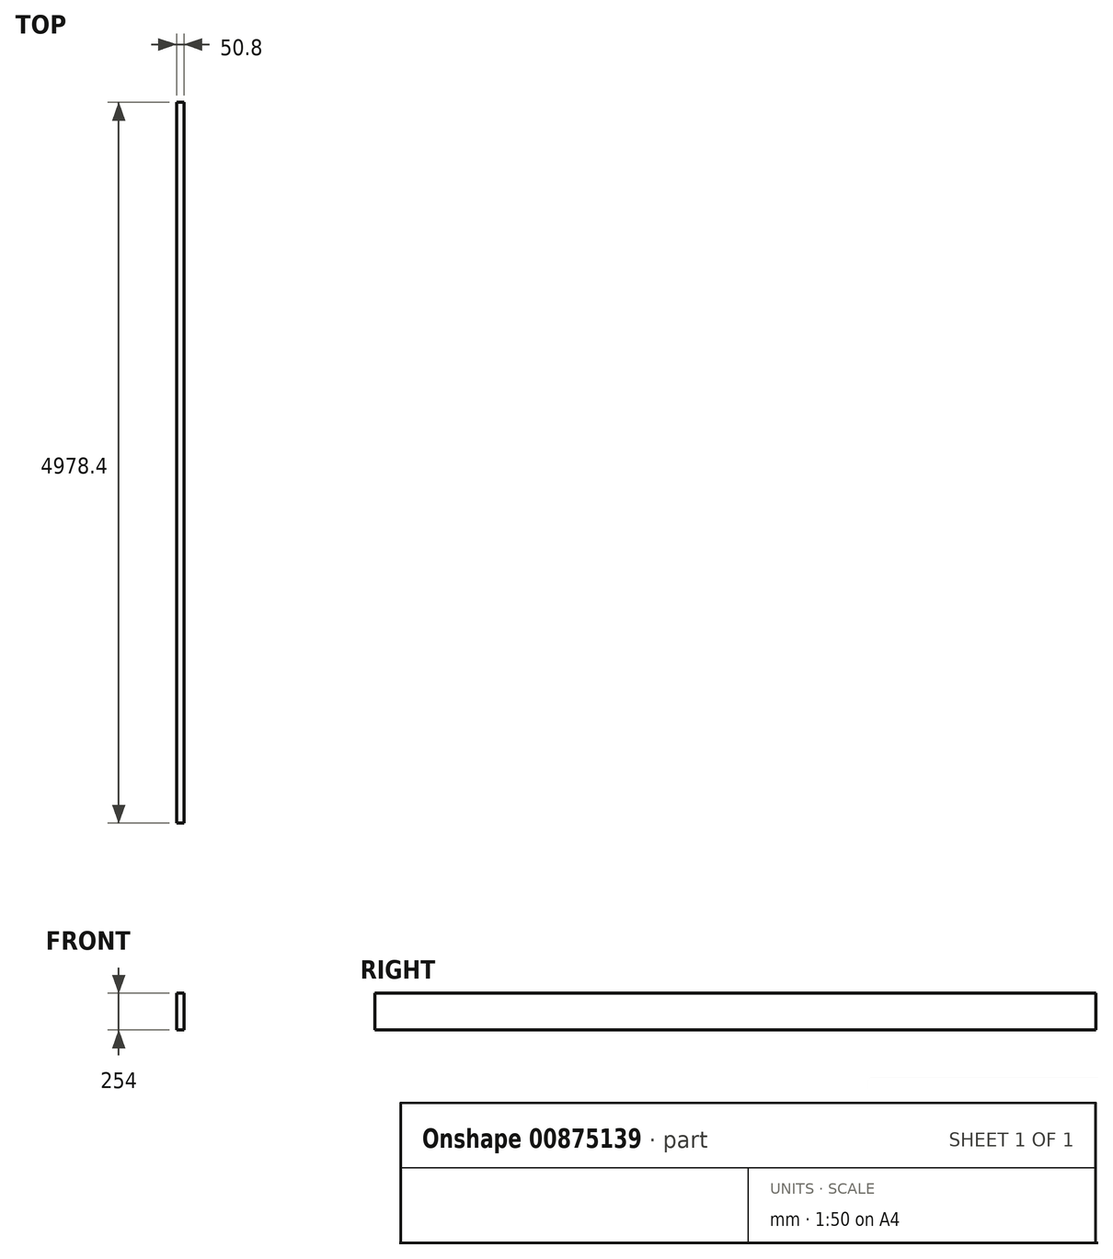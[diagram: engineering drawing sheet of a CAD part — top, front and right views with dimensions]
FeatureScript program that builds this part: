
annotation { "Feature Type Name" : "Feature", "Feature Type Description" : "" }
export const myFeature = defineFeature(function(context is Context, id is Id, definition is map)
    precondition{}
    {
        {
            var Q0;
            Q0=qCreatedBy(makeId("Top.planeOp"),FACE);
            var sketch = newSketch(context, id + "F0", { "sketchPlane" : qUnion([Q0])});
            skLineSegment(sketch, "E0.bottom", {"start": v(-50.8, 0) * mm, "end": v(0, 0) * mm});
            skLineSegment(sketch, "E0.top", {"start": v(-50.8, -4978.4) * mm, "end": v(0, -4978.4) * mm});
            skLineSegment(sketch, "E0.left", {"start": v(-50.8, 0) * mm, "end": v(-50.8, -4978.4) * mm});
            skLineSegment(sketch, "E0.right", {"start": v(0, 0) * mm, "end": v(0, -4978.4) * mm});
            skSolve(sketch);
        }
        {
            var Q0;
            Q0 = qSketchRegion(id + "F0", true);
            extrude(context, id + "F1", {"entities" : qUnion([Q0]), "depth" : 254 * mm, "offsetDistance" : 25.4 * mm});
        }
    });
